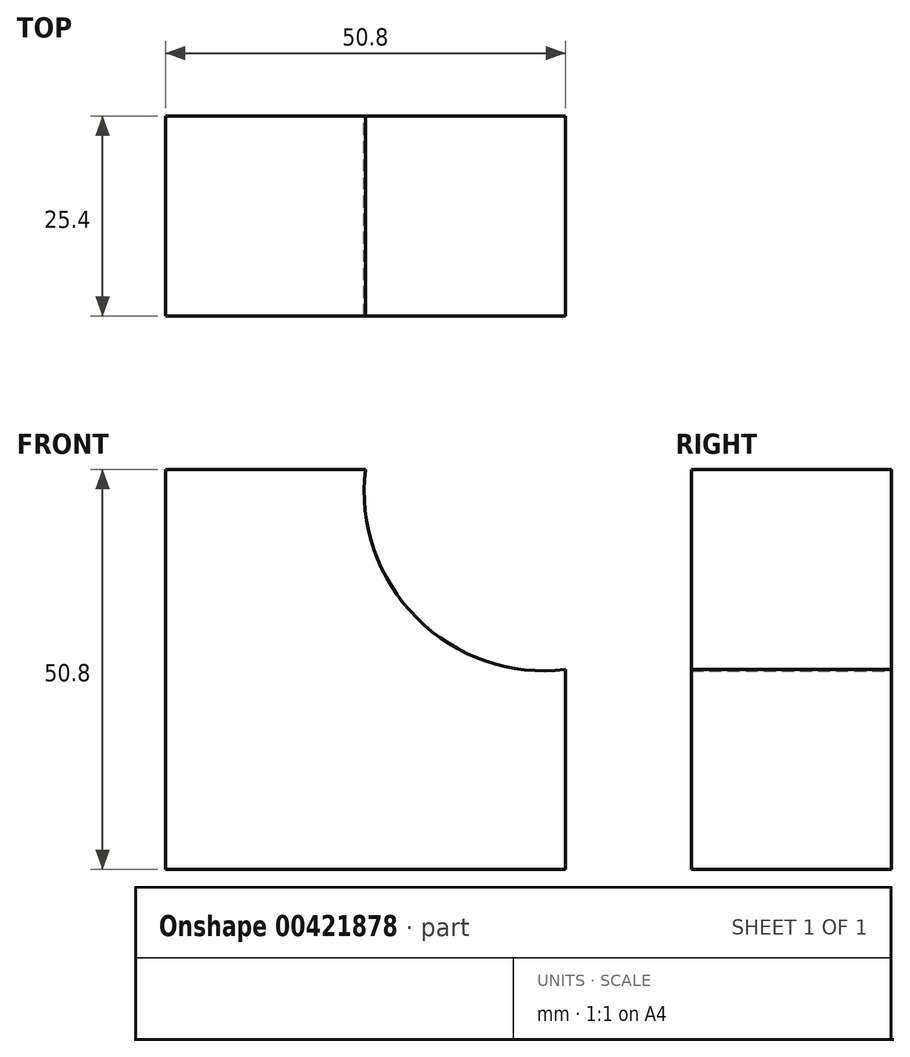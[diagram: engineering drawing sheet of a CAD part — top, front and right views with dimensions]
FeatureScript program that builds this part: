
annotation { "Feature Type Name" : "Feature", "Feature Type Description" : "" }
export const myFeature = defineFeature(function(context is Context, id is Id, definition is map)
    precondition{}
    {
        {
            var Q0;
            Q0=qCreatedBy(makeId("Front.planeOp"),FACE);
            var sketch = newSketch(context, id + "F0", { "sketchPlane" : qUnion([Q0])});
            skLineSegment(sketch, "E0", {"start": v(0, 0) * mm, "end": v(-50.8, 0) * mm});
            skLineSegment(sketch, "E1", {"start": v(-50.8, 0) * mm, "end": v(-50.8, 50.8) * mm});
            skLineSegment(sketch, "E2", {"start": v(-50.8, 50.8) * mm, "end": v(-25.4, 50.8) * mm});
            skLineSegment(sketch, "E3", {"start": v(0, 0) * mm, "end": v(0, 25.4) * mm});
            skArc(sketch, "E4", {"start": v(-25.4, 50.8) * mm, "mid": v(-18.88, 31.92) * mm, "end": v(0, 25.4) * mm});
            skSolve(sketch);
        }
        {
            var Q0;
            Q0 = qSketchRegion(id + "F0", true);
            extrude(context, id + "F1", {"entities" : qUnion([Q0]), "depth" : 25.4 * mm});
        }
    });
